# Revit family: Rough-In_Valve-Temperature_Control-American Standard-R116SS
name_source: partatom
category: Pipe Accessories
units: mm (PartAtom-declared; Revit-internal decimal feet)

## family parameters
Always vertical = Yes
Cut with Voids When Loaded = No
OmniClass Number = 23.65.55.14.24
OmniClass Title = Mixing Valves for Liquid Services
Part Type = Normal
Round Connector Dimension = Use Diameter
Shared = Yes
Work Plane-Based = Yes

## types (1)
- R116SS
    Assembly Code = D2020300
    Default Elevation = 0"
    Description = Pressure Balance Rough Valve Body with Built-In Diverter & Screwdriver stops. LESS Trim.
    Installation Instruction Link = https://lixil.cdn.celum.cloud
    Manufacturer = American Standard
    Material = Cast Iron
    Model = R166SS
    Product Documentation Link = http://www.americanstandard-us.com
    Product URL = https://www.americanstandard.ca
    URL = https://www.americanstandard.ca

## geometry (parser evidence)
native form markers: Sweep x3
no freeform markers — native parametric forms only
